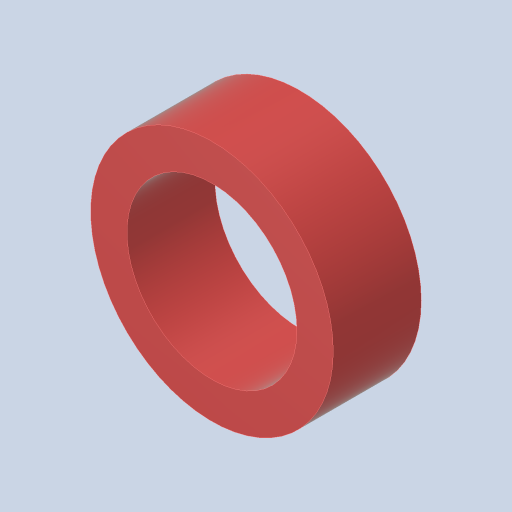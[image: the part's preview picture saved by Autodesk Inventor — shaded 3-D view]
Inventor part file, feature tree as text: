
AUTODESK INVENTOR PART (.ipt)
format: ipt  version: 2023.4 (Build 274418000, 418)  size: 116,224 bytes
history: native  units: in
note: dims shown in document units (in); Inventor stores cm internally (conversion verified against a paired STEP export)
features: extrude x1, sketch x1
ambient origin geometry x8: Origin, YZ Plane, XZ Plane, XY Plane, X Axis, Y Axis, Z Axis, Center Point
bodies: Solid1 (feature_tree)
feature tree (2):
  extrude  "Extrusion1"  Depth=0.303in
  sketch  "Sketch1"  dims[d0=0.585in d1=0.125in d2=0.303in d3=0.0in]
